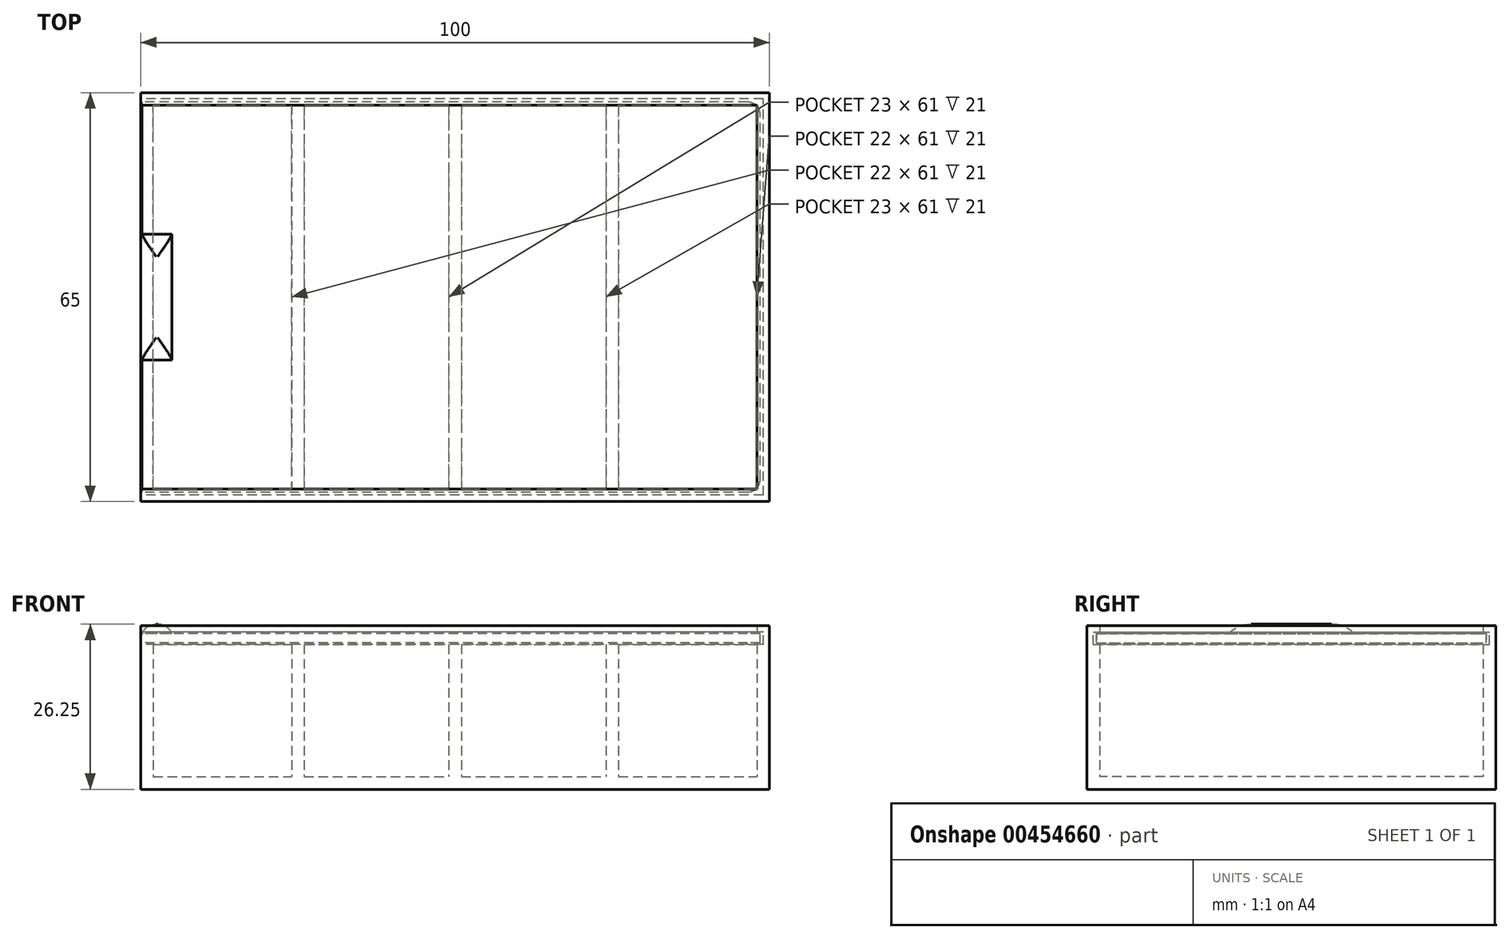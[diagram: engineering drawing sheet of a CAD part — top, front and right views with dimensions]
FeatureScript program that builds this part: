
annotation { "Feature Type Name" : "Feature", "Feature Type Description" : "" }
export const myFeature = defineFeature(function(context is Context, id is Id, definition is map)
    precondition{}
    {
        {
            var Q0;
            Q0=qCreatedBy(makeId("Top.planeOp"),FACE);
            var sketch = newSketch(context, id + "F0", { "sketchPlane" : qUnion([Q0])});
            skLineSegment(sketch, "E0.bottom", {"start": v(0, 0) * mm, "end": v(100, 0) * mm});
            skLineSegment(sketch, "E0.top", {"start": v(0, 65) * mm, "end": v(100, 65) * mm});
            skLineSegment(sketch, "E0.left", {"start": v(0, 0) * mm, "end": v(0, 65) * mm});
            skLineSegment(sketch, "E0.right", {"start": v(100, 0) * mm, "end": v(100, 65) * mm});
            skLineSegment(sketch, "E1.0", {"start": v(2, 63) * mm, "end": v(98, 63) * mm});
            skLineSegment(sketch, "E1.1", {"start": v(2, 2) * mm, "end": v(2, 63) * mm});
            skLineSegment(sketch, "E1.2", {"start": v(2, 2) * mm, "end": v(98, 2) * mm});
            skLineSegment(sketch, "E1.3", {"start": v(98, 2) * mm, "end": v(98, 63) * mm});
            skLineSegment(sketch, "E2.bottom", {"start": v(26, 63) * mm, "end": v(24, 63) * mm});
            skLineSegment(sketch, "E2.top", {"start": v(26, 2) * mm, "end": v(24, 2) * mm});
            skLineSegment(sketch, "E2.left", {"start": v(26, 63) * mm, "end": v(26, 2) * mm});
            skLineSegment(sketch, "E2.right", {"start": v(24, 63) * mm, "end": v(24, 2) * mm});
            skLineSegment(sketch, "E3.1.0.0", {"start": v(49, 63) * mm, "end": v(49, 2) * mm});
            skLineSegment(sketch, "E3.1.0.1", {"start": v(51, 63) * mm, "end": v(51, 2) * mm});
            skLineSegment(sketch, "E3.2.0.0", {"start": v(74, 63) * mm, "end": v(74, 2) * mm});
            skLineSegment(sketch, "E3.2.0.1", {"start": v(76, 63) * mm, "end": v(76, 2) * mm});
            skLineSegment(sketch, "E3.direction1", {"start": v(24, 2) * mm, "end": v(49, 2) * mm, "construction": true});
            skSolve(sketch);
        }
        {
            var Q0;
            Q0=makeQuery(id+"F0.imprint","IMPRINT",FACE,{"disambiguationData":[TD([[makeQuery(id+"F0.imprint","IMPRINT",EDGE,{"derivedFrom":sQuery(id+"F0.wireOp",EDGE,"E0.bottom")}),1.0]])]});
            var Q1;
            {var subQ0=sQuery(id+"F0.wireOp",EDGE,"E2.left");Q1=makeQuery(id+"F0.imprint","IMPRINT",FACE,{"disambiguationData":[TD([[makeQuery(id+"F0.imprint","IMPRINT",EDGE,{"derivedFrom":subQ0}),-1.0]])]});}
            var Q2;
            {var subQ2=sQuery(id+"F0.wireOp",EDGE,"E3.1.0.0");Q2=makeQuery(id+"F0.imprint","IMPRINT",FACE,{"disambiguationData":[TD([[makeQuery(id+"F0.imprint","IMPRINT",EDGE,{"derivedFrom":subQ2}),1.0]])]});}
            var Q3;
            {var subQ0=sQuery(id+"F0.wireOp",EDGE,"E3.2.0.0");Q3=makeQuery(id+"F0.imprint","IMPRINT",FACE,{"disambiguationData":[TD([[makeQuery(id+"F0.imprint","IMPRINT",EDGE,{"derivedFrom":subQ0}),1.0]])]});}
            extrude(context, id + "F1", {"entities" : qUnion([Q0, Q1, Q2, Q3]), "depth" : 26 * mm, "offsetDistance" : 25 * mm});
        }
        {
            var Q0;
            {var subQ0=sQuery(id+"F0.wireOp",EDGE,"E1.1");Q0=makeQuery(id+"F0.imprint","IMPRINT",FACE,{"disambiguationData":[TD([[makeQuery(id+"F0.imprint","IMPRINT",EDGE,{"derivedFrom":subQ0}),-1.0]])]});}
            var Q1;
            {var subQ0=sQuery(id+"F0.wireOp",EDGE,"E2.left");Q1=makeQuery(id+"F0.imprint","IMPRINT",FACE,{"disambiguationData":[TD([[makeQuery(id+"F0.imprint","IMPRINT",EDGE,{"derivedFrom":subQ0}),1.0]])]});}
            var Q2;
            {var subQ0=sQuery(id+"F0.wireOp",EDGE,"E3.1.0.1");Q2=makeQuery(id+"F0.imprint","IMPRINT",FACE,{"disambiguationData":[TD([[makeQuery(id+"F0.imprint","IMPRINT",EDGE,{"derivedFrom":subQ0}),1.0]])]});}
            var Q3;
            {var subQ0=sQuery(id+"F0.wireOp",EDGE,"E1.3");Q3=makeQuery(id+"F0.imprint","IMPRINT",FACE,{"disambiguationData":[TD([[makeQuery(id+"F0.imprint","IMPRINT",EDGE,{"derivedFrom":subQ0}),1.0]])]});}
            extrude(context, id + "F2", {"entities" : qUnion([Q0, Q1, Q2, Q3]), "operationType" : NewBodyOperationType.ADD, "depth" : 2 * mm, "offsetDistance" : 25 * mm});
        }
        {
            var Q0;
            Q0=qCreatedBy(makeId("Right.planeOp"),FACE);
            var sketch = newSketch(context, id + "F3", { "sketchPlane" : qUnion([Q0])});
            skLineSegment(sketch, "E4.bottom", {"start": v(2, 26) * mm, "end": v(63, 26) * mm});
            skLineSegment(sketch, "E4.top", {"start": v(2, 23) * mm, "end": v(63, 23) * mm});
            skLineSegment(sketch, "E4.left", {"start": v(2, 26) * mm, "end": v(2, 23) * mm});
            skLineSegment(sketch, "E4.right", {"start": v(63, 26) * mm, "end": v(63, 23) * mm});
            skPoint(sketch, "E5.oppositeSnap0", {"position": v(63, 25) * mm});
            skLineSegment(sketch, "E5.bottom", {"start": v(63, 23) * mm, "end": v(64, 23) * mm});
            skLineSegment(sketch, "E5.top", {"start": v(63, 25) * mm, "end": v(64, 25) * mm});
            skLineSegment(sketch, "E5.left", {"start": v(63, 23) * mm, "end": v(63, 25) * mm});
            skLineSegment(sketch, "E5.right", {"start": v(64, 23) * mm, "end": v(64, 25) * mm});
            skLineSegment(sketch, "E6", {"start": v(32.5, 26) * mm, "end": v(32.5, -13.48) * mm, "construction": true});
            skLineSegment(sketch, "E7.MirrorCS", {"start": v(2, 25) * mm, "end": v(1, 25) * mm});
            skLineSegment(sketch, "E8.MirrorCS", {"start": v(1, 23) * mm, "end": v(1, 25) * mm});
            skLineSegment(sketch, "E9.MirrorCS", {"start": v(2, 23) * mm, "end": v(1, 23) * mm});
            skLineSegment(sketch, "E10", {"start": v(63, 25) * mm, "end": v(2, 25) * mm});
            skSolve(sketch);
        }
        {
            var Q0;
            {var subQ0=sQuery(id+"F3.wireOp",EDGE,"E4.bottom");Q0=makeQuery(id+"F3.imprint","IMPRINT",FACE,{"disambiguationData":[TD([[makeQuery(id+"F3.imprint","IMPRINT",EDGE,{"derivedFrom":subQ0}),-1.0]])]});}
            extrude(context, id + "F4", {"entities" : qUnion([Q0]), "operationType" : NewBodyOperationType.REMOVE, "depth" : 98 * mm, "offsetDistance" : 25 * mm});
        }
        {
            var Q0;
            {var subQ0=sQuery(id+"F3.wireOp",EDGE,"E5.bottom");Q0=makeQuery(id+"F3.imprint","IMPRINT",FACE,{"disambiguationData":[TD([[makeQuery(id+"F3.imprint","IMPRINT",EDGE,{"derivedFrom":subQ0}),1.0]])]});}
            var Q1;
            {var subQ0=sQuery(id+"F3.wireOp",EDGE,"E4.top");Q1=makeQuery(id+"F3.imprint","IMPRINT",FACE,{"disambiguationData":[TD([[makeQuery(id+"F3.imprint","IMPRINT",EDGE,{"derivedFrom":subQ0}),1.0]])]});}
            var Q2;
            {var subQ2=sQuery(id+"F3.wireOp",EDGE,"E7.MirrorCS");Q2=makeQuery(id+"F3.imprint","IMPRINT",FACE,{"disambiguationData":[TD([[makeQuery(id+"F3.imprint","IMPRINT",EDGE,{"derivedFrom":subQ2}),1.0]])]});}
            extrude(context, id + "F5", {"entities" : qUnion([Q0, Q1, Q2]), "operationType" : NewBodyOperationType.REMOVE, "depth" : 99 * mm, "offsetDistance" : 25 * mm});
        }
        {
            var Q0;
            Q0=qCreatedBy(makeId("Right.planeOp"),FACE);
            var sketch = newSketch(context, id + "F6", { "sketchPlane" : qUnion([Q0])});
            skLineSegment(sketch, "E11", {"start": v(32.5, 28.2) * mm, "end": v(32.5, 24.3) * mm, "construction": true});
            skLineSegment(sketch, "E12", {"start": v(32.5, 24.3) * mm, "end": v(0, 24.3) * mm, "construction": true});
            skPoint(sketch, "E13", {"position": v(32.5, 24) * mm});
            skLineSegment(sketch, "E14.bottom", {"start": v(1.5, 23.25) * mm, "end": v(63.5, 23.25) * mm});
            skLineSegment(sketch, "E14.top", {"start": v(1.5, 24.75) * mm, "end": v(63.5, 24.75) * mm});
            skLineSegment(sketch, "E14.left", {"start": v(1.5, 23.25) * mm, "end": v(1.5, 24.75) * mm});
            skLineSegment(sketch, "E14.right", {"start": v(63.5, 23.25) * mm, "end": v(63.5, 24.75) * mm});
            skLineSegment(sketch, "E15.bottom", {"start": v(42.5, 24.75) * mm, "end": v(22.5, 24.75) * mm});
            skLineSegment(sketch, "E15.top", {"start": v(42.5, 26.25) * mm, "end": v(22.5, 26.25) * mm});
            skLineSegment(sketch, "E15.left", {"start": v(42.5, 24.75) * mm, "end": v(42.5, 26.25) * mm});
            skLineSegment(sketch, "E15.right", {"start": v(22.5, 24.75) * mm, "end": v(22.5, 26.25) * mm});
            skPoint(sketch, "E16", {"position": v(32.5, 26.25) * mm});
            skSolve(sketch);
        }
        {
            var Q0;
            Q0=makeQuery(id+"F6.imprint","IMPRINT",FACE,{"disambiguationData":[TD([[makeQuery(id+"F6.imprint","IMPRINT",EDGE,{"derivedFrom":sQuery(id+"F6.wireOp",EDGE,"E14.bottom")}),1.0]])]});
            extrude(context, id + "F7", {"entities" : qUnion([Q0]), "depth" : 98.5 * mm, "offsetDistance" : 25 * mm});
        }
        {
            var Q0;
            Q0=makeQuery(id+"F6.imprint","IMPRINT",FACE,{"disambiguationData":[TD([[makeQuery(id+"F6.imprint","IMPRINT",EDGE,{"derivedFrom":sQuery(id+"F6.wireOp",EDGE,"E15.top")}),1.0]])]});
            extrude(context, id + "F8", {"entities" : qUnion([Q0]), "operationType" : NewBodyOperationType.ADD, "depth" : 5 * mm, "offsetDistance" : 25 * mm});
        }
        {
            var Q0;
            Q0=makeQuery(id+"F8.opExtrude","CAP_EDGE",EDGE,{"disambiguationData":[OSD([sQuery(id+"F6.wireOp",EDGE,"E15.top")])],"isStart":false});
            var Q1;
            Q1=makeQuery(id+"F8.opExtrude","CAP_EDGE",EDGE,{"disambiguationData":[OSD([sQuery(id+"F6.wireOp",EDGE,"E15.top")])],"isStart":true});
            fillet(context, id + "F9", {"entities" : qUnion([Q0, Q1]), "tangentPropagation" : true, "radius" : 2.5 * mm, "defaultsChanged" : true, "vertexSettings" : [], "allowEdgeOverflow" : false});
        }
        {
            var Q0;
            Q0=makeQuery(id+"F7.opExtrude","CAP_EDGE",EDGE,{"disambiguationData":[OSD([sQuery(id+"F6.wireOp",EDGE,"E14.left")])],"isStart":false});
            var Q1;
            Q1=makeQuery(id+"F7.opExtrude","CAP_EDGE",EDGE,{"disambiguationData":[OSD([sQuery(id+"F6.wireOp",EDGE,"E14.right")])],"isStart":false});
            fillet(context, id + "F10", {"entities" : qUnion([Q0, Q1]), "tangentPropagation" : true, "radius" : 2 * mm, "defaultsChanged" : true, "vertexSettings" : [], "allowEdgeOverflow" : false});
        }
        {
            var Q0;
            Q0=makeQuery(id+"F8.opExtrude","SWEPT_EDGE",EDGE,{"disambiguationData":[OSD([sQuery(id+"F6.wireOp",EDGE,"E15.top"),sQuery(id+"F6.wireOp",EDGE,"E15.right")])]});
            var Q1;
            Q1=makeQuery(id+"F8.opExtrude","SWEPT_EDGE",EDGE,{"disambiguationData":[OSD([sQuery(id+"F6.wireOp",EDGE,"E15.top"),sQuery(id+"F6.wireOp",EDGE,"E15.left")])]});
            fillet(context, id + "F11", {"entities" : qUnion([Q0, Q1]), "tangentPropagation" : true, "radius" : 5 * mm, "defaultsChanged" : false, "vertexSettings" : [], "allowEdgeOverflow" : false});
        }
    });
